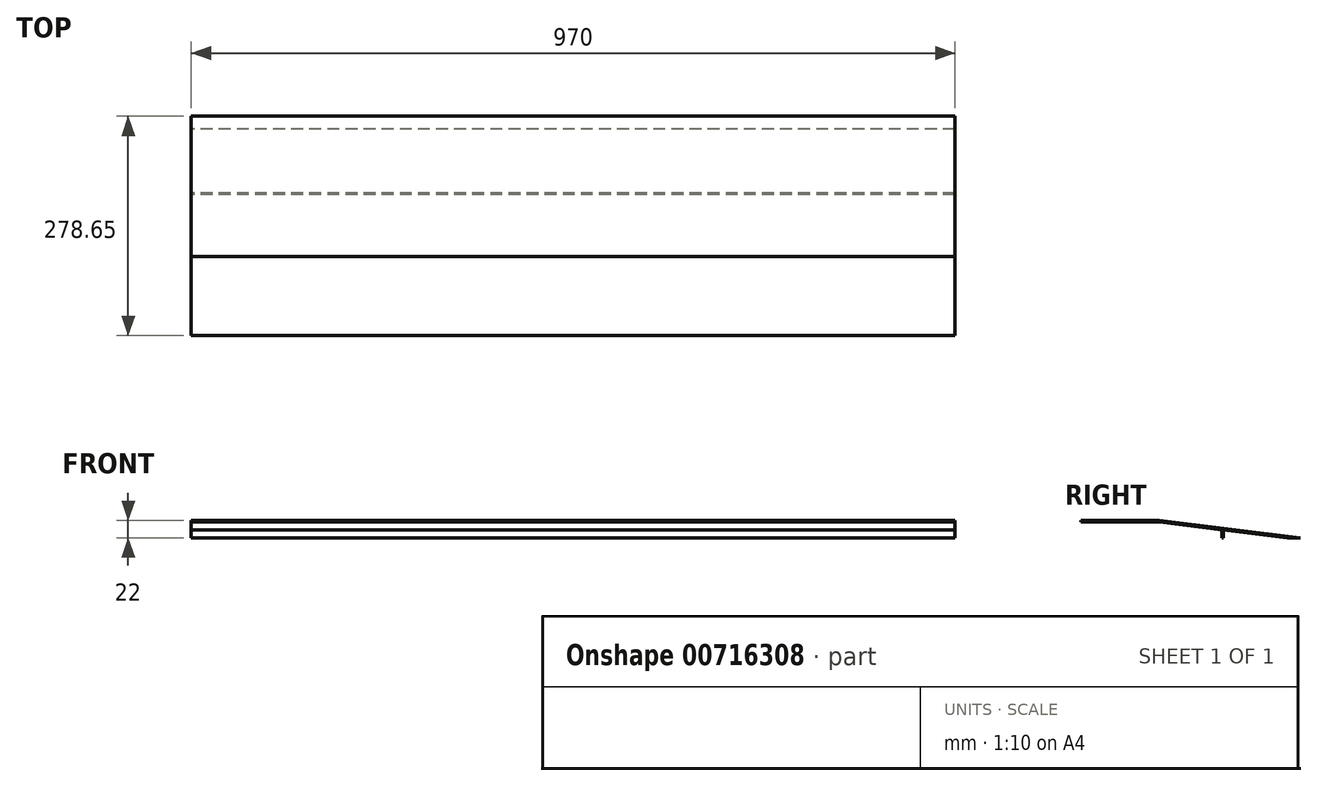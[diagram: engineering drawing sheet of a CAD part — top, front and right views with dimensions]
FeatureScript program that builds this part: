
annotation { "Feature Type Name" : "Feature", "Feature Type Description" : "" }
export const myFeature = defineFeature(function(context is Context, id is Id, definition is map)
    precondition{}
    {
        {
            var Q0;
            Q0=qCreatedBy(makeId("Right.planeOp"),FACE);
            var sketch = newSketch(context, id + "F0", { "sketchPlane" : qUnion([Q0])});
            skLineSegment(sketch, "E0.bottom", {"start": v(0, 0) * mm, "end": v(2.3, 0) * mm});
            skLineSegment(sketch, "E0.top", {"start": v(0, 20) * mm, "end": v(30, 20) * mm});
            skLineSegment(sketch, "E0.left", {"start": v(0, 0) * mm, "end": v(0, 20) * mm});
            skLineSegment(sketch, "E0.right", {"start": v(30, 0) * mm, "end": v(30, 20) * mm});
            skLineSegment(sketch, "E1.0", {"start": v(27.7, 0) * mm, "end": v(27.7, 17.7) * mm});
            skLineSegment(sketch, "E2.0", {"start": v(2.3, 17.7) * mm, "end": v(27.7, 17.7) * mm});
            skLineSegment(sketch, "E3.0", {"start": v(2.3, 0) * mm, "end": v(2.3, 17.7) * mm});
            skLineSegment(sketch, "E4.trimOffspring", {"start": v(27.7, 0) * mm, "end": v(30, 0) * mm});
            skSolve(sketch);
        }
        {
            var Q0;
            Q0=qSketchRegion(id+"F0",true);
            extrude(context, id + "F1", {"entities" : qUnion([Q0]), "depth" : 970 * mm, "offsetDistance" : 25 * mm});
        }
        {
            var Q0;
            Q0=makeQuery(id+"F1.opExtrude","SWEPT_FACE",FACE,{"disambiguationData":[OSD([sQuery(id+"F0.wireOp",EDGE,"E0.top")])]});
            var sketch = newSketch(context, id + "F2", { "sketchPlane" : qUnion([Q0])});
            skLineSegment(sketch, "E5.bottom", {"start": v(0, 0) * mm, "end": v(35, 0) * mm});
            skLineSegment(sketch, "E5.top", {"start": v(0, 30) * mm, "end": v(35, 30) * mm});
            skLineSegment(sketch, "E5.left", {"start": v(0, 0) * mm, "end": v(0, 30) * mm});
            skLineSegment(sketch, "E5.right", {"start": v(35, 0) * mm, "end": v(35, 30) * mm});
            skLineSegment(sketch, "E6.bottom", {"start": v(970, 0) * mm, "end": v(935, 0) * mm});
            skLineSegment(sketch, "E6.top", {"start": v(970, 30) * mm, "end": v(935, 30) * mm});
            skLineSegment(sketch, "E6.left", {"start": v(970, 0) * mm, "end": v(970, 30) * mm});
            skLineSegment(sketch, "E6.right", {"start": v(935, 0) * mm, "end": v(935, 30) * mm});
            skSolve(sketch);
        }
        {
            var Q0;
            Q0=qSketchRegion(id+"F2",true);
            extrude(context, id + "F3", {"entities" : qUnion([Q0]), "operationType" : NewBodyOperationType.REMOVE, "oppositeDirection" : true, "depth" : 2.3 * mm, "offsetDistance" : 25 * mm});
        }
        {
            var Q0;
            Q0=makeQuery(id+"F1.opExtrude","SWEPT_FACE",FACE,{"disambiguationData":[OSD([sQuery(id+"F0.wireOp",EDGE,"E0.left")])]});
            var sketch = newSketch(context, id + "F4", { "sketchPlane" : qUnion([Q0])});
            skLineSegment(sketch, "E7.bottom", {"start": v(35, 0) * mm, "end": v(32.6, 0) * mm});
            skLineSegment(sketch, "E7.top", {"start": v(35, 1) * mm, "end": v(32.6, 1) * mm});
            skLineSegment(sketch, "E7.left", {"start": v(35, 0) * mm, "end": v(35, 1) * mm});
            skLineSegment(sketch, "E7.right", {"start": v(32.6, 0) * mm, "end": v(32.6, 1) * mm});
            skLineSegment(sketch, "E8.bottom", {"start": v(7.4, 0) * mm, "end": v(5, 0) * mm});
            skLineSegment(sketch, "E8.top", {"start": v(7.4, 1) * mm, "end": v(5, 1) * mm});
            skLineSegment(sketch, "E8.left", {"start": v(7.4, 0) * mm, "end": v(7.4, 1) * mm});
            skLineSegment(sketch, "E8.right", {"start": v(5, 0) * mm, "end": v(5, 1) * mm});
            skLineSegment(sketch, "E9", {"start": v(485, 128) * mm, "end": v(485, 0) * mm, "construction": true});
            skLineSegment(sketch, "E10.MirrorCS", {"start": v(937.4, 0) * mm, "end": v(937.4, 1) * mm});
            skLineSegment(sketch, "E11.MirrorCS", {"start": v(935, 1) * mm, "end": v(937.4, 1) * mm});
            skLineSegment(sketch, "E12.MirrorCS", {"start": v(935, 0) * mm, "end": v(935, 1) * mm});
            skLineSegment(sketch, "E13.MirrorCS", {"start": v(965, 0) * mm, "end": v(965, 1) * mm});
            skLineSegment(sketch, "E14.MirrorCS", {"start": v(962.6, 1) * mm, "end": v(965, 1) * mm});
            skLineSegment(sketch, "E15.MirrorCS", {"start": v(962.6, 0) * mm, "end": v(962.6, 1) * mm});
            skLineSegment(sketch, "E16.MirrorCS", {"start": v(962.6, 0) * mm, "end": v(965, 0) * mm});
            skLineSegment(sketch, "E17.MirrorCS", {"start": v(935, 0) * mm, "end": v(937.4, 0) * mm});
            skSolve(sketch);
        }
        {
            var Q0;
            Q0=qSketchRegion(id+"F4",true);
            extrude(context, id + "F5", {"entities" : qUnion([Q0]), "operationType" : NewBodyOperationType.REMOVE, "endBound" : BoundingType.THROUGH_ALL, "oppositeDirection" : true, "depth" : 25 * mm, "offsetDistance" : 25 * mm});
        }
        {
            var Q0;
            Q0=qCreatedBy(makeId("Right.planeOp"),FACE);
            var sketch = newSketch(context, id + "F6", { "sketchPlane" : qUnion([Q0])});
            skLineSegment(sketch, "E18.bottom", {"start": v(95, 20) * mm, "end": v(-5, 20) * mm});
            skLineSegment(sketch, "E18.top", {"start": v(95, 22) * mm, "end": v(-5, 22) * mm});
            skLineSegment(sketch, "E19", {"start": v(95, 22) * mm, "end": v(273.65, 0) * mm});
            skLineSegment(sketch, "E20", {"start": v(95, 20) * mm, "end": v(257.4, 0) * mm});
            skLineSegment(sketch, "E21", {"start": v(257.4, 0) * mm, "end": v(273.65, 0) * mm});
            skLineSegment(sketch, "E22", {"start": v(0, 0) * mm, "end": v(226.36, 0) * mm, "construction": true});
            skLineSegment(sketch, "E23", {"start": v(176.2, 10) * mm, "end": v(176.2, 0) * mm});
            skLineSegment(sketch, "E24", {"start": v(174.2, 10.25) * mm, "end": v(174.2, 0) * mm});
            skLineSegment(sketch, "E25", {"start": v(174.2, 0) * mm, "end": v(176.2, 0) * mm});
            skLineSegment(sketch, "E26", {"start": v(15, 37) * mm, "end": v(15, -23.89) * mm, "construction": true});
            skLineSegment(sketch, "E27", {"start": v(-5, 22) * mm, "end": v(-5, 20) * mm});
            skSolve(sketch);
        }
        {
            var Q0;
            Q0=qSketchRegion(id+"F6",true);
            extrude(context, id + "F7", {"entities" : qUnion([Q0]), "depth" : 970 * mm, "offsetDistance" : 25 * mm});
        }
        {
            var Q0;
            Q0=makeQuery(id+"F1.opExtrude","SWEPT_BODY",BODY,{"disambiguationData":[OSD([sQuery(id+"F0.wireOp",EDGE,"E0.bottom"),sQuery(id+"F0.wireOp",EDGE,"E0.top"),sQuery(id+"F0.wireOp",EDGE,"E0.left"),sQuery(id+"F0.wireOp",EDGE,"E0.right"),sQuery(id+"F0.wireOp",EDGE,"E1.0"),sQuery(id+"F0.wireOp",EDGE,"E2.0"),sQuery(id+"F0.wireOp",EDGE,"E3.0"),sQuery(id+"F0.wireOp",EDGE,"E4.trimOffspring")])]});
            deleteBodies(context, id + "F8", {"entities" : qUnion([Q0])});
        }
    });
